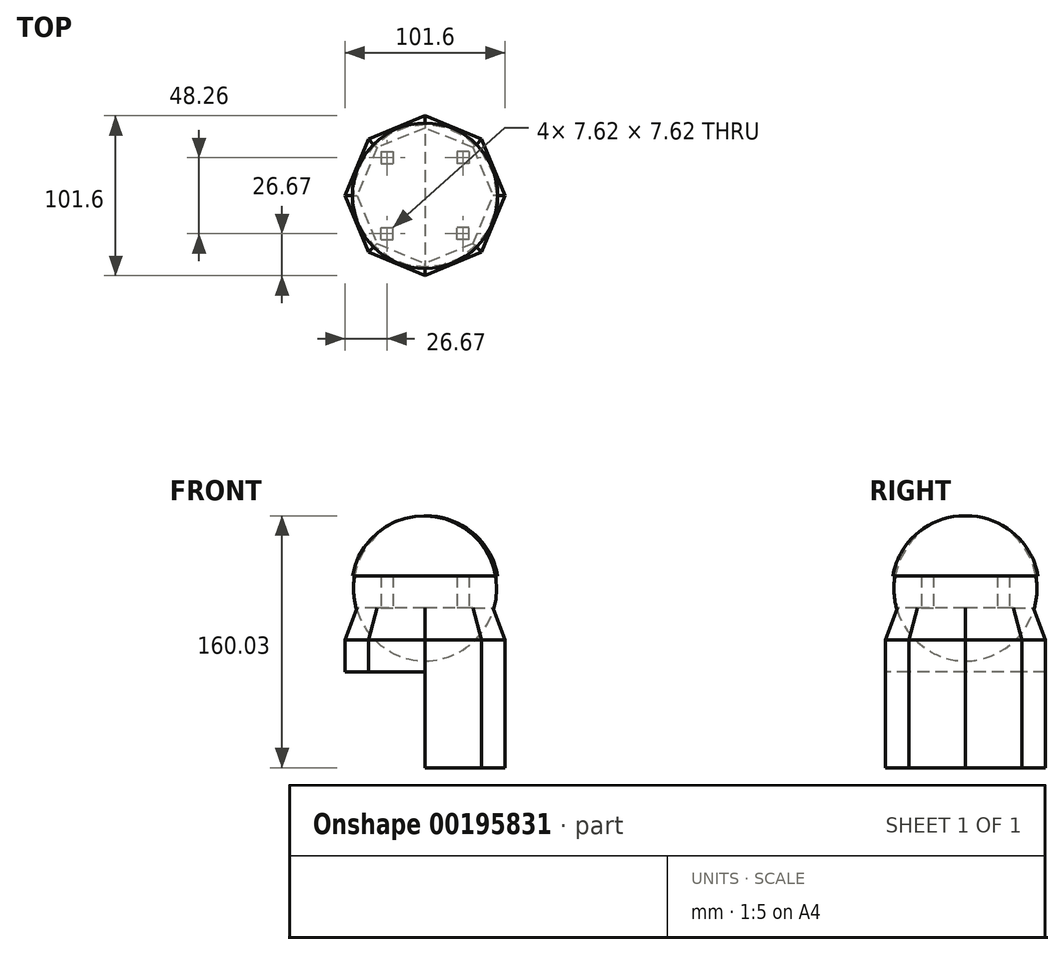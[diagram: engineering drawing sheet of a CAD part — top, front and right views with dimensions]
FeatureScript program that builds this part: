
annotation { "Feature Type Name" : "Feature", "Feature Type Description" : "" }
export const myFeature = defineFeature(function(context is Context, id is Id, definition is map)
    precondition{}
    {
        {
            var Q0;
            Q0=qCreatedBy(makeId("Top.planeOp"),FACE);
            var sketch = newSketch(context, id + "F0", { "sketchPlane" : qUnion([Q0])});
            skLineSegment(sketch, "E0", {"start": v(0, 50.8) * mm, "end": v(0, -50.8) * mm});
            skArc(sketch, "E1", {"start": v(0, -50.8) * mm, "mid": v(50.8, 0) * mm, "end": v(0, 50.8) * mm, "construction": true});
            skLineSegment(sketch, "E2", {"start": v(0, 50.8) * mm, "end": v(35.92, 35.92) * mm});
            skLineSegment(sketch, "E3", {"start": v(35.92, 35.92) * mm, "end": v(50.8, 0) * mm});
            skLineSegment(sketch, "E4", {"start": v(50.8, 0) * mm, "end": v(35.92, -35.92) * mm});
            skLineSegment(sketch, "E5", {"start": v(35.92, -35.92) * mm, "end": v(0, -50.8) * mm});
            skSolve(sketch);
        }
        {
            var Q0;
            Q0=qCreatedBy(makeId("Top.planeOp"),FACE);
            cPlane(context, id + "F1", {"entities" : qUnion([Q0]), "cplaneType" : CPlaneType.OFFSET, "offset" : 60.96 * mm, "width" : 152.4 * mm, "height" : 152.4 * mm});
        }
        {
            var Q0;
            Q0=makeQuery(id+"F0.imprint","IMPRINT",FACE,{"disambiguationData":[TD([[makeQuery(id+"F0.imprint","IMPRINT",EDGE,{"derivedFrom":sQuery(id+"F0.wireOp",EDGE,"E0")}),1.0]])]});
            extrude(context, id + "F2", {"entities" : qUnion([Q0]), "depth" : 60.96 * mm});
        }
        {
            var Q0;
            Q0=qCreatedBy(id+"F1.planeOp",FACE);
            var sketch = newSketch(context, id + "F3", { "sketchPlane" : qUnion([Q0])});
            skCircle(sketch, "E6", {"center": v(0, 0) * mm, "radius": 50.8 * mm, "construction": true});
            skLineSegment(sketch, "E7.0", {"start": v(0, 50.8) * mm, "end": v(35.92, 35.92) * mm});
            skLineSegment(sketch, "E8.0", {"start": v(35.92, 35.92) * mm, "end": v(50.8, 0) * mm});
            skLineSegment(sketch, "E9.0", {"start": v(50.8, 0) * mm, "end": v(35.92, -35.92) * mm});
            skLineSegment(sketch, "E10.0", {"start": v(35.92, -35.92) * mm, "end": v(0, -50.8) * mm});
            skLineSegment(sketch, "E11", {"start": v(0, 50.8) * mm, "end": v(-35.92, 35.92) * mm});
            skLineSegment(sketch, "E12", {"start": v(-35.92, 35.92) * mm, "end": v(-50.8, 0) * mm});
            skLineSegment(sketch, "E13", {"start": v(-50.8, 0) * mm, "end": v(-35.92, -35.92) * mm});
            skLineSegment(sketch, "E14", {"start": v(-35.92, -35.92) * mm, "end": v(0, -50.8) * mm});
            skSolve(sketch);
        }
        {
            var Q0;
            Q0=makeQuery(id+"F3.imprint","IMPRINT",FACE,{"disambiguationData":[TD([[makeQuery(id+"F3.imprint","IMPRINT",EDGE,{"derivedFrom":sQuery(id+"F3.wireOp",EDGE,"E7.0")}),-1.0]])]});
            extrude(context, id + "F4", {"entities" : qUnion([Q0]), "operationType" : NewBodyOperationType.ADD, "depth" : 20.32 * mm});
        }
        {
            var Q0;
            Q0=qCreatedBy(id+"F1.planeOp",FACE);
            cPlane(context, id + "F5", {"entities" : qUnion([Q0]), "cplaneType" : CPlaneType.OFFSET, "offset" : 40.64 * mm, "width" : 152.4 * mm, "height" : 152.4 * mm});
        }
        {
            var Q0;
            Q0=makeQuery(id+"F4.opExtrude","CAP_FACE",FACE,{"disambiguationData":[OSD([sQuery(id+"F3.wireOp",EDGE,"E7.0"),sQuery(id+"F3.wireOp",EDGE,"E8.0"),sQuery(id+"F3.wireOp",EDGE,"E9.0"),sQuery(id+"F3.wireOp",EDGE,"E10.0"),sQuery(id+"F3.wireOp",EDGE,"E11"),sQuery(id+"F3.wireOp",EDGE,"E12"),sQuery(id+"F3.wireOp",EDGE,"E13"),sQuery(id+"F3.wireOp",EDGE,"E14")])],"isStart":false});
            cPlane(context, id + "F6", {"entities" : qUnion([Q0]), "cplaneType" : CPlaneType.OFFSET, "offset" : 0 * mm, "width" : 152.4 * mm, "height" : 152.4 * mm});
        }
        {
            var Q0;
            Q0=qCreatedBy(id+"F6.planeOp",FACE);
            var sketch = newSketch(context, id + "F7", { "sketchPlane" : qUnion([Q0])});
            skLineSegment(sketch, "E15.0", {"start": v(-35.92, 35.92) * mm, "end": v(-50.8, 0) * mm});
            skLineSegment(sketch, "E16.0", {"start": v(0, 50.8) * mm, "end": v(-35.92, 35.92) * mm});
            skLineSegment(sketch, "E17.0", {"start": v(-50.8, 0) * mm, "end": v(-35.92, -35.92) * mm});
            skLineSegment(sketch, "E18.0", {"start": v(-35.92, -35.92) * mm, "end": v(0, -50.8) * mm});
            skLineSegment(sketch, "E19.0", {"start": v(35.92, -35.92) * mm, "end": v(0, -50.8) * mm});
            skLineSegment(sketch, "E20.0", {"start": v(50.8, 0) * mm, "end": v(35.92, -35.92) * mm});
            skLineSegment(sketch, "E21.0", {"start": v(35.92, 35.92) * mm, "end": v(50.8, 0) * mm});
            skLineSegment(sketch, "E22.0", {"start": v(0, 50.8) * mm, "end": v(35.92, 35.92) * mm});
            skSolve(sketch);
        }
        {
            var Q0;
            Q0=qCreatedBy(id+"F5.planeOp",FACE);
            var sketch = newSketch(context, id + "F8", { "sketchPlane" : qUnion([Q0])});
            skLineSegment(sketch, "E23.bottom", {"start": v(-30.48, 30.48) * mm, "end": v(30.48, 30.48) * mm, "construction": true});
            skLineSegment(sketch, "E23.top", {"start": v(-30.48, -30.48) * mm, "end": v(30.48, -30.48) * mm, "construction": true});
            skLineSegment(sketch, "E23.left", {"start": v(-30.48, 30.48) * mm, "end": v(-30.48, -30.48) * mm, "construction": true});
            skLineSegment(sketch, "E23.right", {"start": v(30.48, 30.48) * mm, "end": v(30.48, -30.48) * mm, "construction": true});
            skPoint(sketch, "E23.middle", {"position": v(0, 0) * mm});
            skLineSegment(sketch, "E24", {"start": v(30.48, 30.48) * mm, "end": v(0, 43.1) * mm});
            skLineSegment(sketch, "E25", {"start": v(0, 43.1) * mm, "end": v(-30.48, 30.48) * mm});
            skLineSegment(sketch, "E26", {"start": v(-30.48, 30.48) * mm, "end": v(-43.1, 0) * mm});
            skLineSegment(sketch, "E27", {"start": v(-43.1, 0) * mm, "end": v(-30.48, -30.48) * mm});
            skLineSegment(sketch, "E28", {"start": v(-30.48, -30.48) * mm, "end": v(0, -43.1) * mm});
            skLineSegment(sketch, "E29", {"start": v(30.48, -30.48) * mm, "end": v(0, -43.1) * mm});
            skLineSegment(sketch, "E30", {"start": v(30.48, -30.48) * mm, "end": v(43.1, 0) * mm});
            skLineSegment(sketch, "E31", {"start": v(30.48, 30.48) * mm, "end": v(43.1, 0) * mm});
            skPoint(sketch, "E32.0", {"position": v(35.92, 35.92) * mm});
            skLineSegment(sketch, "E33", {"start": v(35.92, 35.92) * mm, "end": v(30.48, 30.48) * mm, "construction": true});
            skPoint(sketch, "E34.0", {"position": v(0, 50.8) * mm});
            skPoint(sketch, "E35.0", {"position": v(-35.92, 35.92) * mm});
            skPoint(sketch, "E36.0", {"position": v(-50.8, 0) * mm});
            skPoint(sketch, "E37.0", {"position": v(-35.92, -35.92) * mm});
            skPoint(sketch, "E38.0", {"position": v(0, -50.8) * mm});
            skPoint(sketch, "E39.0", {"position": v(35.92, -35.92) * mm});
            skPoint(sketch, "E40.0", {"position": v(50.8, 0) * mm});
            skLineSegment(sketch, "E41", {"start": v(50.8, 0) * mm, "end": v(43.1, 0) * mm, "construction": true});
            skLineSegment(sketch, "E42", {"start": v(30.48, -30.48) * mm, "end": v(35.92, -35.92) * mm, "construction": true});
            skLineSegment(sketch, "E43", {"start": v(0, -43.1) * mm, "end": v(0, -50.8) * mm, "construction": true});
            skLineSegment(sketch, "E44", {"start": v(-30.48, -30.48) * mm, "end": v(-35.92, -35.92) * mm, "construction": true});
            skLineSegment(sketch, "E45", {"start": v(-50.8, 0) * mm, "end": v(-43.1, 0) * mm, "construction": true});
            skLineSegment(sketch, "E46", {"start": v(-35.92, 35.92) * mm, "end": v(-30.48, 30.48) * mm, "construction": true});
            skLineSegment(sketch, "E47", {"start": v(0, 43.1) * mm, "end": v(0, 50.8) * mm, "construction": true});
            skLineSegment(sketch, "E48", {"start": v(35.92, 35.92) * mm, "end": v(50.8, 0) * mm, "construction": true});
            skLineSegment(sketch, "E49", {"start": v(50.8, 0) * mm, "end": v(35.92, -35.92) * mm, "construction": true});
            skLineSegment(sketch, "E50", {"start": v(35.92, -35.92) * mm, "end": v(0, -50.8) * mm, "construction": true});
            skLineSegment(sketch, "E51", {"start": v(0, -50.8) * mm, "end": v(-35.92, -35.92) * mm, "construction": true});
            skLineSegment(sketch, "E52", {"start": v(-35.92, -35.92) * mm, "end": v(-50.8, 0) * mm, "construction": true});
            skLineSegment(sketch, "E53", {"start": v(-50.8, 0) * mm, "end": v(-35.92, 35.92) * mm, "construction": true});
            skLineSegment(sketch, "E54", {"start": v(-35.92, 35.92) * mm, "end": v(0, 50.8) * mm, "construction": true});
            skLineSegment(sketch, "E55", {"start": v(0, 50.8) * mm, "end": v(35.92, 35.92) * mm, "construction": true});
            skSolve(sketch);
        }
        {
            var Q0;
            Q0=qCreatedBy(id+"F5.planeOp",FACE);
            var sketch = newSketch(context, id + "F9", { "sketchPlane" : qUnion([Q0])});
            skLineSegment(sketch, "E56.bottom", {"start": v(-30.48, 30.48) * mm, "end": v(30.48, 30.48) * mm, "construction": true});
            skLineSegment(sketch, "E56.top", {"start": v(-30.48, -30.48) * mm, "end": v(30.48, -30.48) * mm, "construction": true});
            skLineSegment(sketch, "E56.left", {"start": v(-30.48, 30.48) * mm, "end": v(-30.48, -30.48) * mm, "construction": true});
            skLineSegment(sketch, "E56.right", {"start": v(30.48, 30.48) * mm, "end": v(30.48, -30.48) * mm, "construction": true});
            skPoint(sketch, "E56.middle", {"position": v(0, 0) * mm});
            skLineSegment(sketch, "E57", {"start": v(0, 30.48) * mm, "end": v(0, -30.48) * mm, "construction": true});
            skLineSegment(sketch, "E58", {"start": v(30.48, 0) * mm, "end": v(-30.48, 0) * mm, "construction": true});
            skLineSegment(sketch, "E59.bottom", {"start": v(-27.94, 27.94) * mm, "end": v(-20.32, 27.94) * mm});
            skLineSegment(sketch, "E59.top", {"start": v(-27.94, 20.32) * mm, "end": v(-20.32, 20.32) * mm});
            skLineSegment(sketch, "E59.left", {"start": v(-27.94, 27.94) * mm, "end": v(-27.94, 20.32) * mm});
            skLineSegment(sketch, "E59.right", {"start": v(-20.32, 27.94) * mm, "end": v(-20.32, 20.32) * mm});
            skLineSegment(sketch, "E60.MirrorCS", {"start": v(20.32, 27.94) * mm, "end": v(20.32, 20.32) * mm});
            skLineSegment(sketch, "E61.MirrorCS", {"start": v(27.94, 27.94) * mm, "end": v(20.32, 27.94) * mm});
            skLineSegment(sketch, "E62.MirrorCS", {"start": v(27.94, 27.94) * mm, "end": v(27.94, 20.32) * mm});
            skLineSegment(sketch, "E63.MirrorCS", {"start": v(27.94, 20.32) * mm, "end": v(20.32, 20.32) * mm});
            skLineSegment(sketch, "E64.MirrorCS", {"start": v(-27.94, -20.32) * mm, "end": v(-20.32, -20.32) * mm});
            skLineSegment(sketch, "E65.MirrorCS", {"start": v(-20.32, -27.94) * mm, "end": v(-20.32, -20.32) * mm});
            skLineSegment(sketch, "E66.MirrorCS", {"start": v(-27.94, -27.94) * mm, "end": v(-27.94, -20.32) * mm});
            skLineSegment(sketch, "E67.MirrorCS", {"start": v(-27.94, -27.94) * mm, "end": v(-20.32, -27.94) * mm});
            skLineSegment(sketch, "E68.MirrorCS", {"start": v(20.32, -27.94) * mm, "end": v(20.32, -20.32) * mm});
            skLineSegment(sketch, "E69.MirrorCS", {"start": v(27.94, -27.94) * mm, "end": v(20.32, -27.94) * mm});
            skLineSegment(sketch, "E70.MirrorCS", {"start": v(27.94, -27.94) * mm, "end": v(27.94, -20.32) * mm});
            skLineSegment(sketch, "E71.MirrorCS", {"start": v(27.94, -20.32) * mm, "end": v(20.32, -20.32) * mm});
            skSolve(sketch);
        }
        {
            var Q0;
            Q0=qCreatedBy(id+"F5.planeOp",FACE);
            cPlane(context, id + "F10", {"entities" : qUnion([Q0]), "cplaneType" : CPlaneType.OFFSET, "offset" : 20.32 * mm, "width" : 152.4 * mm, "height" : 152.4 * mm});
        }
        {
            var Q0;
            Q0=qCreatedBy(id+"F10.planeOp",FACE);
            var sketch = newSketch(context, id + "F11", { "sketchPlane" : qUnion([Q0])});
            skCircle(sketch, "E72", {"center": v(0, 0) * mm, "radius": 46.16 * mm});
            skLineSegment(sketch, "E73.0", {"start": v(0, 43.1) * mm, "end": v(-30.48, 30.48) * mm, "construction": true});
            skLineSegment(sketch, "E74.0", {"start": v(-30.48, 30.48) * mm, "end": v(-43.1, 0) * mm, "construction": true});
            skLineSegment(sketch, "E75", {"start": v(0, 0) * mm, "end": v(-46.16, 0) * mm, "construction": true});
            skLineSegment(sketch, "E76", {"start": v(0, 0) * mm, "end": v(0, 46.16) * mm, "construction": true});
            skLineSegment(sketch, "E77", {"start": v(-46.16, 0) * mm, "end": v(-32.64, 32.64) * mm, "construction": true});
            skLineSegment(sketch, "E78", {"start": v(-32.64, 32.64) * mm, "end": v(0, 46.16) * mm, "construction": true});
            skLineSegment(sketch, "E79", {"start": v(0, 46.16) * mm, "end": v(32.64, 32.64) * mm, "construction": true});
            skLineSegment(sketch, "E80", {"start": v(32.64, 32.64) * mm, "end": v(46.16, 0) * mm, "construction": true});
            skLineSegment(sketch, "E81", {"start": v(-46.16, 0) * mm, "end": v(-32.64, -32.64) * mm, "construction": true});
            skLineSegment(sketch, "E82", {"start": v(-32.64, -32.64) * mm, "end": v(0, -46.16) * mm, "construction": true});
            skLineSegment(sketch, "E83", {"start": v(0, -46.16) * mm, "end": v(32.64, -32.64) * mm, "construction": true});
            skLineSegment(sketch, "E84", {"start": v(32.64, -32.64) * mm, "end": v(46.16, 0) * mm, "construction": true});
            skSolve(sketch);
        }
        {
            var Q0;
            Q0=qCreatedBy(id+"F10.planeOp",FACE);
            cPlane(context, id + "F12", {"entities" : qUnion([Q0]), "cplaneType" : CPlaneType.OFFSET, "offset" : 12.7 * mm, "width" : 152.4 * mm, "height" : 152.4 * mm});
        }
        {
            var Q1;
            Q1 = qSketchRegion(id + "F7", true);
            var Q2;
            Q2 = qSketchRegion(id + "F8", true);
            loft(context, id + "F13", {"operationType" : NewBodyOperationType.ADD, "sheetProfilesArray" : [{ "sheetProfileEntities" : qUnion([Q1]) }, { "sheetProfileEntities" : qUnion([Q2]) }]});
        }
        {
            var Q0;
            Q0 = qSketchRegion(id + "F9", true);
            extrude(context, id + "F14", {"entities" : qUnion([Q0]), "operationType" : NewBodyOperationType.ADD, "depth" : 20.32 * mm});
        }
        {
            var Q0;
            Q0=qCreatedBy(makeId("Front.planeOp"),FACE);
            var sketch = newSketch(context, id + "F15", { "sketchPlane" : qUnion([Q0])});
            skLineSegment(sketch, "E85.0", {"start": v(-46.16, 121.92) * mm, "end": v(46.16, 121.92) * mm});
            skPoint(sketch, "E86", {"position": v(0, 121.92) * mm});
            skLineSegment(sketch, "E87", {"start": v(0, 121.92) * mm, "end": v(0, 160.02) * mm});
            skArc(sketch, "E88", {"start": v(0, 160.02) * mm, "mid": v(-30.1, 149.47) * mm, "end": v(-46.16, 121.92) * mm});
            skSolve(sketch);
        }
        {
            var Q0;
            {var subQ2=sQuery(id+"F15.wireOp",EDGE,"E87");Q0=makeQuery(id+"F15.imprint","IMPRINT",FACE,{"disambiguationData":[TD([[makeQuery(id+"F15.imprint","IMPRINT",EDGE,{"derivedFrom":subQ2}),1.0]])]});}
            var Q1;
            Q1=sQuery(id+"F15.wireOp",EDGE,"E87");
            revolve(context, id + "F16", {"operationType" : NewBodyOperationType.ADD, "entities" : qUnion([Q0]), "axis" : qUnion([Q1]), "revolveType" : RevolveType.FULL});
        }
        {
            var Q0;
            Q0=makeQuery(id+"F13.opLoft","CAP_FACE",FACE,{"disambiguationData":[OSD([makeQuery(id+"F8.imprint","IMPRINT",FACE,{"disambiguationData":[TD([[makeQuery(id+"F8.imprint","IMPRINT",EDGE,{"derivedFrom":sQuery(id+"F8.wireOp",EDGE,"E24")}),1.0]])]})])],"isStart":true});
            var sketch = newSketch(context, id + "F17", { "sketchPlane" : qUnion([Q0])});
            skLineSegment(sketch, "E89.0", {"start": v(-30.48, 30.48) * mm, "end": v(-43.1, 0) * mm, "construction": true});
            skLineSegment(sketch, "E90.0", {"start": v(0, 43.1) * mm, "end": v(-30.48, 30.48) * mm, "construction": true});
            skLineSegment(sketch, "E91.0", {"start": v(30.48, 30.48) * mm, "end": v(0, 43.1) * mm, "construction": true});
            skLineSegment(sketch, "E92.0", {"start": v(43.1, 0) * mm, "end": v(30.48, 30.48) * mm, "construction": true});
            skLineSegment(sketch, "E93.0", {"start": v(30.48, -30.48) * mm, "end": v(43.1, 0) * mm, "construction": true});
            skLineSegment(sketch, "E94.0", {"start": v(0, -43.1) * mm, "end": v(30.48, -30.48) * mm, "construction": true});
            skLineSegment(sketch, "E95.0", {"start": v(-30.48, -30.48) * mm, "end": v(0, -43.1) * mm, "construction": true});
            skLineSegment(sketch, "E96.0", {"start": v(-43.1, 0) * mm, "end": v(-30.48, -30.48) * mm, "construction": true});
            skSolve(sketch);
        }
        {
            var Q0;
            Q0=makeQuery(id+"F13.opLoft","SWEPT_FACE",FACE,{"disambiguationData":[OSD([sQuery(id+"F7.wireOp",EDGE,"E18.0"),sQuery(id+"F7.wireOp",EDGE,"E19.0"),sQuery(id+"F7.wireOp",EDGE,"E20.0"),sQuery(id+"F8.wireOp",EDGE,"E28"),sQuery(id+"F8.wireOp",EDGE,"E29"),sQuery(id+"F8.wireOp",EDGE,"E30")])]});
            cPlane(context, id + "F18", {"entities" : qUnion([Q0]), "cplaneType" : CPlaneType.OFFSET, "offset" : 0 * mm, "width" : 152.4 * mm, "height" : 152.4 * mm});
        }
    });
